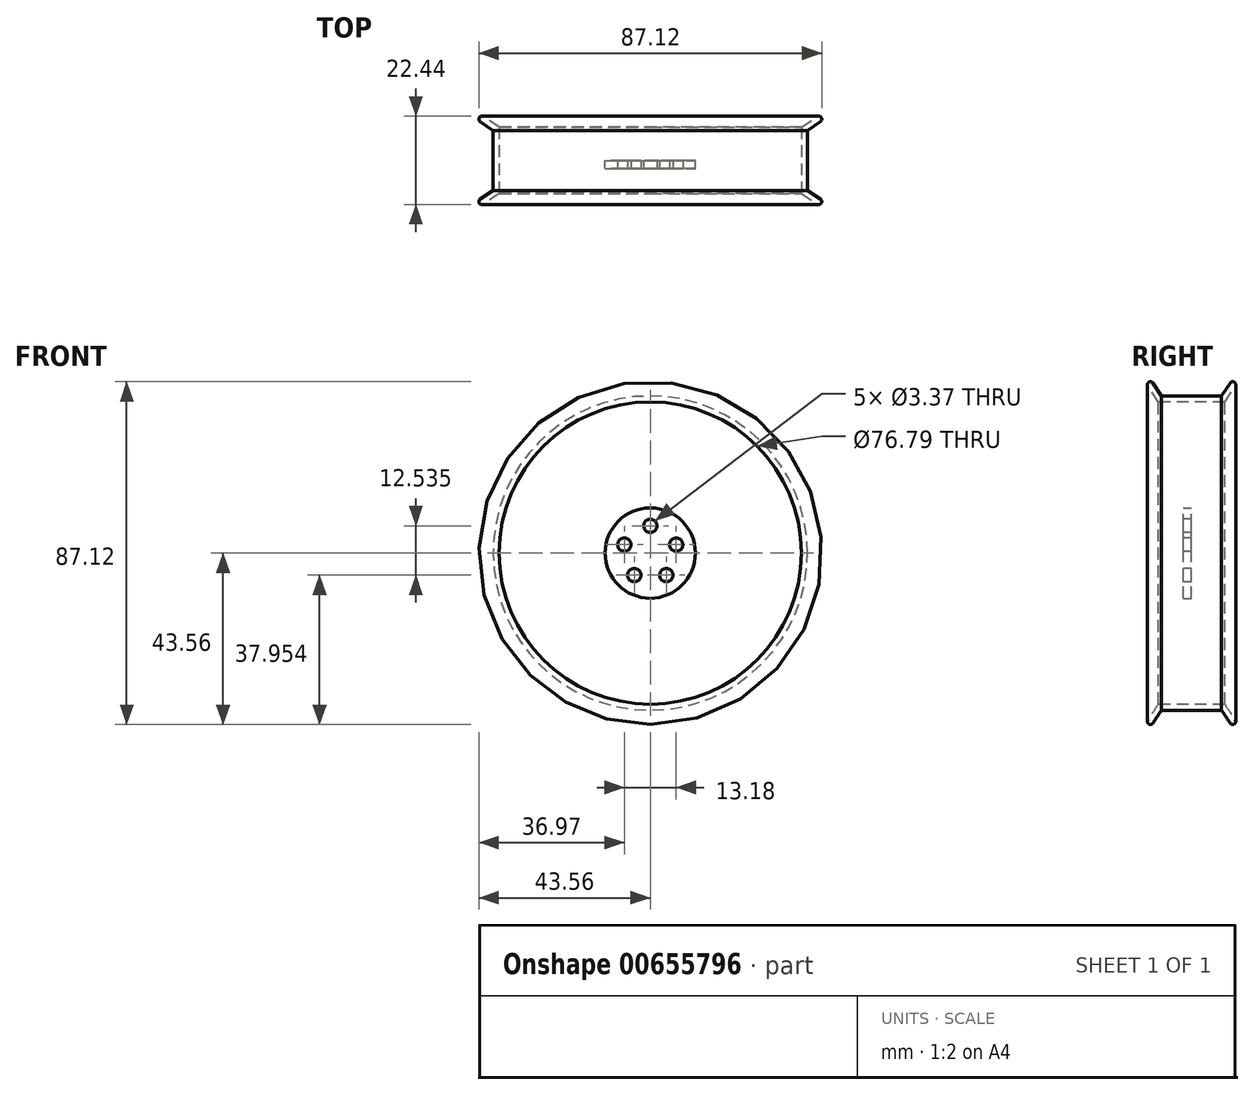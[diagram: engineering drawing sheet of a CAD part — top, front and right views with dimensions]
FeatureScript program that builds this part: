
annotation { "Feature Type Name" : "Feature", "Feature Type Description" : "" }
export const myFeature = defineFeature(function(context is Context, id is Id, definition is map)
    precondition{}
    {
        {
            var Q0;
            Q0=qCreatedBy(makeId("Right.planeOp"),FACE);
            var sketch = newSketch(context, id + "F0", { "sketchPlane" : qUnion([Q0])});
            skLineSegment(sketch, "E0", {"start": v(8.44, 38.4) * mm, "end": v(11.1, 42.37) * mm});
            skLineSegment(sketch, "E1", {"start": v(8.44, 38.4) * mm, "end": v(0, 38.4) * mm});
            skLineSegment(sketch, "E2.MirrorCS", {"start": v(-8.44, 38.4) * mm, "end": v(0, 38.4) * mm});
            skLineSegment(sketch, "E3.MirrorCS", {"start": v(-8.44, 38.4) * mm, "end": v(-11.1, 42.37) * mm});
            skLineSegment(sketch, "E4.0", {"start": v(-7.62, 39.92) * mm, "end": v(-9.82, 43.22) * mm});
            skLineSegment(sketch, "E4.1", {"start": v(-7.62, 39.92) * mm, "end": v(0, 39.92) * mm});
            skLineSegment(sketch, "E4.2", {"start": v(7.62, 39.92) * mm, "end": v(0, 39.92) * mm});
            skLineSegment(sketch, "E4.3", {"start": v(7.62, 39.92) * mm, "end": v(9.82, 43.22) * mm});
            skArc(sketch, "E5", {"start": v(11.1, 42.37) * mm, "mid": v(10.88, 43.43) * mm, "end": v(9.82, 43.22) * mm});
            skArc(sketch, "E6", {"start": v(-9.82, 43.22) * mm, "mid": v(-10.88, 43.43) * mm, "end": v(-11.1, 42.37) * mm});
            skSolve(sketch);
        }
        {
            var Q0;
            Q0=qCreatedBy(makeId("Right.planeOp"),FACE);
            var sketch = newSketch(context, id + "F1", { "sketchPlane" : qUnion([Q0])});
            skLineSegment(sketch, "E7", {"start": v(-20, 0) * mm, "end": v(19.24, 0) * mm});
            skSolve(sketch);
        }
        {
            var Q0;
            Q0=makeQuery(id+"F0.imprint","IMPRINT",FACE,{"disambiguationData":[TD([[makeQuery(id+"F0.imprint","IMPRINT",EDGE,{"derivedFrom":sQuery(id+"F0.wireOp",EDGE,"E0")}),1.0]])]});
            var Q1;
            Q1=sQuery(id+"F1.wireOp",EDGE,"E7");
            revolve(context, id + "F2", {"entities" : qUnion([Q0]), "axis" : qUnion([Q1]), "revolveType" : RevolveType.FULL});
        }
        {
            var Q0;
            Q0=qCreatedBy(makeId("Front.planeOp"),FACE);
            var sketch = newSketch(context, id + "F3", { "sketchPlane" : qUnion([Q0])});
            skCircle(sketch, "E8", {"center": v(0, 0) * mm, "radius": 11.47 * mm});
            skSolve(sketch);
        }
        {
            var Q0;
            Q0=makeQuery(id+"F3.imprint","IMPRINT",FACE,{"disambiguationData":[TD([[makeQuery(id+"F3.imprint","IMPRINT",EDGE,{"derivedFrom":sQuery(id+"F3.wireOp",EDGE,"E8")}),1.0]])]});
            extrude(context, id + "F4", {"entities" : qUnion([Q0]), "depth" : 2.03 * mm, "offsetDistance" : 25.4 * mm});
        }
        {
            var Q0;
            Q0=makeQuery(id+"F4.opExtrude","CAP_FACE",FACE,{"disambiguationData":[OSD([sQuery(id+"F3.wireOp",EDGE,"E8")])],"isStart":false});
            var sketch = newSketch(context, id + "F5", { "sketchPlane" : qUnion([Q0])});
            skCircle(sketch, "E9", {"center": v(0, 6.93) * mm, "radius": 1.68 * mm});
            skCircle(sketch, "E10.1.0", {"center": v(-6.6, 2.14) * mm, "radius": 1.68 * mm});
            skCircle(sketch, "E10.2.0", {"center": v(-4.07, -5.6) * mm, "radius": 1.68 * mm});
            skCircle(sketch, "E10.3.0", {"center": v(4.07, -5.6) * mm, "radius": 1.68 * mm});
            skCircle(sketch, "E10.4.0", {"center": v(6.6, 2.14) * mm, "radius": 1.68 * mm});
            skPoint(sketch, "E10.center", {"position": v(0, 0) * mm});
            skSolve(sketch);
        }
        {
            var Q0;
            Q0=makeQuery(id+"F5.imprint","IMPRINT",FACE,{"disambiguationData":[TD([[makeQuery(id+"F5.imprint","IMPRINT",EDGE,{"derivedFrom":sQuery(id+"F5.wireOp",EDGE,"E9")}),1.0]])]});
            var Q1;
            Q1=makeQuery(id+"F5.imprint","IMPRINT",FACE,{"disambiguationData":[TD([[makeQuery(id+"F5.imprint","IMPRINT",EDGE,{"derivedFrom":sQuery(id+"F5.wireOp",EDGE,"E10.4.0")}),1.0]])]});
            var Q2;
            Q2=makeQuery(id+"F5.imprint","IMPRINT",FACE,{"disambiguationData":[TD([[makeQuery(id+"F5.imprint","IMPRINT",EDGE,{"derivedFrom":sQuery(id+"F5.wireOp",EDGE,"E10.3.0")}),1.0]])]});
            var Q3;
            Q3=makeQuery(id+"F5.imprint","IMPRINT",FACE,{"disambiguationData":[TD([[makeQuery(id+"F5.imprint","IMPRINT",EDGE,{"derivedFrom":sQuery(id+"F5.wireOp",EDGE,"E10.2.0")}),1.0]])]});
            var Q4;
            Q4=makeQuery(id+"F5.imprint","IMPRINT",FACE,{"disambiguationData":[TD([[makeQuery(id+"F5.imprint","IMPRINT",EDGE,{"derivedFrom":sQuery(id+"F5.wireOp",EDGE,"E10.1.0")}),1.0]])]});
            extrude(context, id + "F6", {"entities" : qUnion([Q0, Q1, Q2, Q3, Q4]), "operationType" : NewBodyOperationType.REMOVE, "endBound" : BoundingType.THROUGH_ALL, "oppositeDirection" : true, "depth" : 25.4 * mm, "offsetDistance" : 25.4 * mm});
        }
    });
